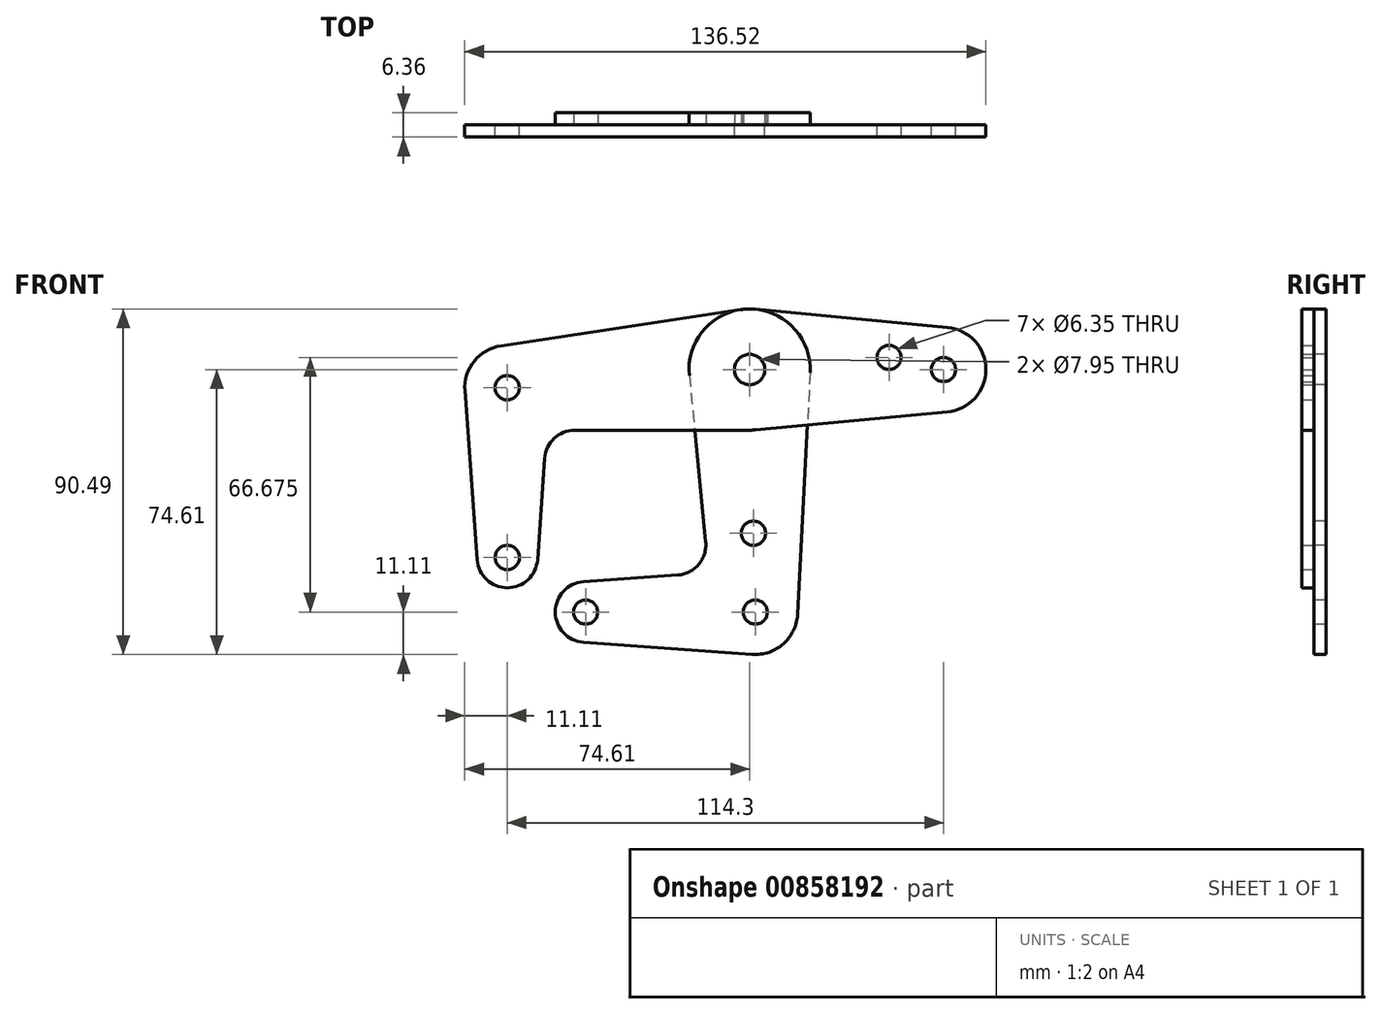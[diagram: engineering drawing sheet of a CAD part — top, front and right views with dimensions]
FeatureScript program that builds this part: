
annotation { "Feature Type Name" : "Feature", "Feature Type Description" : "" }
export const myFeature = defineFeature(function(context is Context, id is Id, definition is map)
    precondition{}
    {
        {
            var Q0;
            Q0=qCreatedBy(makeId("Front.planeOp"),FACE);
            var sketch = newSketch(context, id + "F0", { "sketchPlane" : qUnion([Q0])});
            skCircle(sketch, "E0", {"center": v(0, 0) * mm, "radius": 15.88 * mm});
            skCircle(sketch, "E1", {"center": v(50.8, 0) * mm, "radius": 11.11 * mm});
            skCircle(sketch, "E2", {"center": v(-63.5, -4.76) * mm, "radius": 11.11 * mm});
            skCircle(sketch, "E3", {"center": v(50.8, 0) * mm, "radius": 3.18 * mm});
            skCircle(sketch, "E4", {"center": v(36.53, 3.17) * mm, "radius": 3.18 * mm});
            skCircle(sketch, "E5", {"center": v(-63.47, -49.21) * mm, "radius": 7.94 * mm});
            skCircle(sketch, "E6", {"center": v(-63.5, -4.76) * mm, "radius": 3.18 * mm});
            skCircle(sketch, "E7", {"center": v(-63.47, -49.21) * mm, "radius": 3.18 * mm});
            skCircle(sketch, "E8", {"center": v(0, 0) * mm, "radius": 3.98 * mm});
            skLineSegment(sketch, "E9", {"start": v(-53.67, -23.26) * mm, "end": v(-55.55, -49.77) * mm});
            skLineSegment(sketch, "E10", {"start": v(-74.58, -5.56) * mm, "end": v(-71.38, -49.79) * mm});
            skLineSegment(sketch, "E11", {"start": v(-65.16, 6.23) * mm, "end": v(0, 16.05) * mm});
            skLineSegment(sketch, "E12", {"start": v(0, -15.87) * mm, "end": v(-45.74, -15.88) * mm});
            skLineSegment(sketch, "E13", {"start": v(-0.01, 15.95) * mm, "end": v(51.84, 11.06) * mm});
            skLineSegment(sketch, "E14", {"start": v(1.49, -15.8) * mm, "end": v(51.84, -11.06) * mm});
            skArc(sketch, "E15.filletArc", {"start": v(-45.74, -15.88) * mm, "mid": v(-51.16, -18) * mm, "end": v(-53.67, -23.26) * mm});
            skCircle(sketch, "E16", {"center": v(1.49, -63.5) * mm, "radius": 11.11 * mm});
            skCircle(sketch, "E17", {"center": v(1, -42.85) * mm, "radius": 3.18 * mm});
            skCircle(sketch, "E18", {"center": v(-42.96, -63.5) * mm, "radius": 7.94 * mm});
            skCircle(sketch, "E19", {"center": v(-42.96, -63.5) * mm, "radius": 3.18 * mm});
            skCircle(sketch, "E20", {"center": v(1.49, -63.5) * mm, "radius": 3.18 * mm});
            skLineSegment(sketch, "E21", {"start": v(-15.8, -1.56) * mm, "end": v(-11.5, -45.1) * mm});
            skLineSegment(sketch, "E22", {"start": v(15.85, -0.82) * mm, "end": v(12.59, -64.07) * mm});
            skLineSegment(sketch, "E23", {"start": v(-43.53, -55.58) * mm, "end": v(-18.84, -53.81) * mm});
            skLineSegment(sketch, "E24", {"start": v(-43.53, -71.42) * mm, "end": v(0.7, -74.58) * mm});
            skArc(sketch, "E25.filletArc", {"start": v(-18.84, -53.81) * mm, "mid": v(-13.33, -51) * mm, "end": v(-11.5, -45.1) * mm});
            skSolve(sketch);
        }
        {
            var Q0;
            Q0=makeQuery(id+"F0.imprint","IMPRINT",FACE,{"disambiguationData":[TD([[makeQuery(id+"F0.imprint","IMPRINT",EDGE,{"derivedFrom":sQuery(id+"F0.wireOp",EDGE,"E3")}),-1.0]])]});
            var Q1;
            Q1=makeQuery(id+"F0.imprint","IMPRINT",FACE,{"disambiguationData":[TD([[makeQuery(id+"F0.imprint","IMPRINT",EDGE,{"derivedFrom":sQuery(id+"F0.wireOp",EDGE,"E6")}),-1.0]])]});
            var Q2;
            Q2=makeQuery(id+"F0.imprint","IMPRINT",FACE,{"disambiguationData":[TD([[makeQuery(id+"F0.imprint","IMPRINT",EDGE,{"derivedFrom":sQuery(id+"F0.wireOp",EDGE,"E7")}),-1.0]])]});
            var Q3;
            {var subQ0=sQuery(id+"F0.wireOp",EDGE,"E14");var subQ1=sQuery(id+"F0.wireOp",EDGE,"E0");var subQ2=makeQuery(id+"F0.imprint","INTERSECT",VERTEX,{"derivedFrom":[subQ1,subQ0]});Q3=makeQuery(id+"F0.imprint","IMPRINT",FACE,{"disambiguationData":[TD([[makeQuery(id+"F0.imprint","IMPRINT",EDGE,{"disambiguationData":[TD([[subQ2,-1.0]])],"derivedFrom":subQ1}),-1.0]])]});}
            var Q4;
            {var subQ0=sQuery(id+"F0.wireOp",EDGE,"E9");Q4=makeQuery(id+"F0.imprint","IMPRINT",FACE,{"disambiguationData":[TD([[makeQuery(id+"F0.imprint","IMPRINT",EDGE,{"derivedFrom":subQ0}),-1.0]])]});}
            var Q5;
            Q5=makeQuery(id+"F0.imprint","IMPRINT",FACE,{"disambiguationData":[TD([[makeQuery(id+"F0.imprint","IMPRINT",EDGE,{"derivedFrom":sQuery(id+"F0.wireOp",EDGE,"E4")}),-1.0]])]});
            var Q6;
            Q6=makeQuery(id+"F0.imprint","IMPRINT",FACE,{"disambiguationData":[TD([[makeQuery(id+"F0.imprint","IMPRINT",EDGE,{"derivedFrom":sQuery(id+"F0.wireOp",EDGE,"E8")}),-1.0]])]});
            var Q7;
            {var subQ0=sQuery(id+"F0.wireOp",EDGE,"E12");var subQ1=sQuery(id+"F0.wireOp",EDGE,"E0");var subQ2=makeQuery(id+"F0.imprint","INTERSECT",VERTEX,{"derivedFrom":[subQ1,subQ0]});Q7=makeQuery(id+"F0.imprint","IMPRINT",FACE,{"disambiguationData":[TD([[makeQuery(id+"F0.imprint","IMPRINT",EDGE,{"disambiguationData":[TD([[subQ2,1.0]])],"derivedFrom":subQ1}),-1.0]])]});}
            extrude(context, id + "F1", {"entities" : qUnion([Q0, Q1, Q2, Q3, Q4, Q5, Q6, Q7]), "depth" : 3.17 * mm, "offsetDistance" : 25.4 * mm});
        }
        {
            var Q0;
            Q0=makeQuery(id+"F0.imprint","IMPRINT",FACE,{"disambiguationData":[TD([[makeQuery(id+"F0.imprint","IMPRINT",EDGE,{"derivedFrom":sQuery(id+"F0.wireOp",EDGE,"E17")}),-1.0]])]});
            var Q1;
            Q1=makeQuery(id+"F0.imprint","IMPRINT",FACE,{"disambiguationData":[TD([[makeQuery(id+"F0.imprint","IMPRINT",EDGE,{"derivedFrom":sQuery(id+"F0.wireOp",EDGE,"E20")}),-1.0]])]});
            var Q2;
            Q2=makeQuery(id+"F0.imprint","IMPRINT",FACE,{"disambiguationData":[TD([[makeQuery(id+"F0.imprint","IMPRINT",EDGE,{"derivedFrom":sQuery(id+"F0.wireOp",EDGE,"E19")}),-1.0]])]});
            var Q3;
            Q3=makeQuery(id+"F0.imprint","IMPRINT",FACE,{"disambiguationData":[TD([[makeQuery(id+"F0.imprint","IMPRINT",EDGE,{"derivedFrom":sQuery(id+"F0.wireOp",EDGE,"E8")}),-1.0]])]});
            var Q4;
            {var subQ0=sQuery(id+"F0.wireOp",EDGE,"E14");var subQ1=sQuery(id+"F0.wireOp",EDGE,"E0");var subQ2=makeQuery(id+"F0.imprint","INTERSECT",VERTEX,{"derivedFrom":[subQ1,subQ0]});Q4=makeQuery(id+"F0.imprint","IMPRINT",FACE,{"disambiguationData":[TD([[makeQuery(id+"F0.imprint","IMPRINT",EDGE,{"disambiguationData":[TD([[subQ2,-1.0]])],"derivedFrom":subQ1}),-1.0]])]});}
            var Q5;
            {var subQ0=sQuery(id+"F0.wireOp",EDGE,"E12");var subQ1=sQuery(id+"F0.wireOp",EDGE,"E0");var subQ2=makeQuery(id+"F0.imprint","INTERSECT",VERTEX,{"derivedFrom":[subQ1,subQ0]});Q5=makeQuery(id+"F0.imprint","IMPRINT",FACE,{"disambiguationData":[TD([[makeQuery(id+"F0.imprint","IMPRINT",EDGE,{"disambiguationData":[TD([[subQ2,1.0]])],"derivedFrom":subQ1}),-1.0]])]});}
            extrude(context, id + "F2", {"entities" : qUnion([Q0, Q1, Q2, Q3, Q4, Q5]), "oppositeDirection" : true, "depth" : 3.17 * mm, "offsetDistance" : 25.4 * mm});
        }
    });
